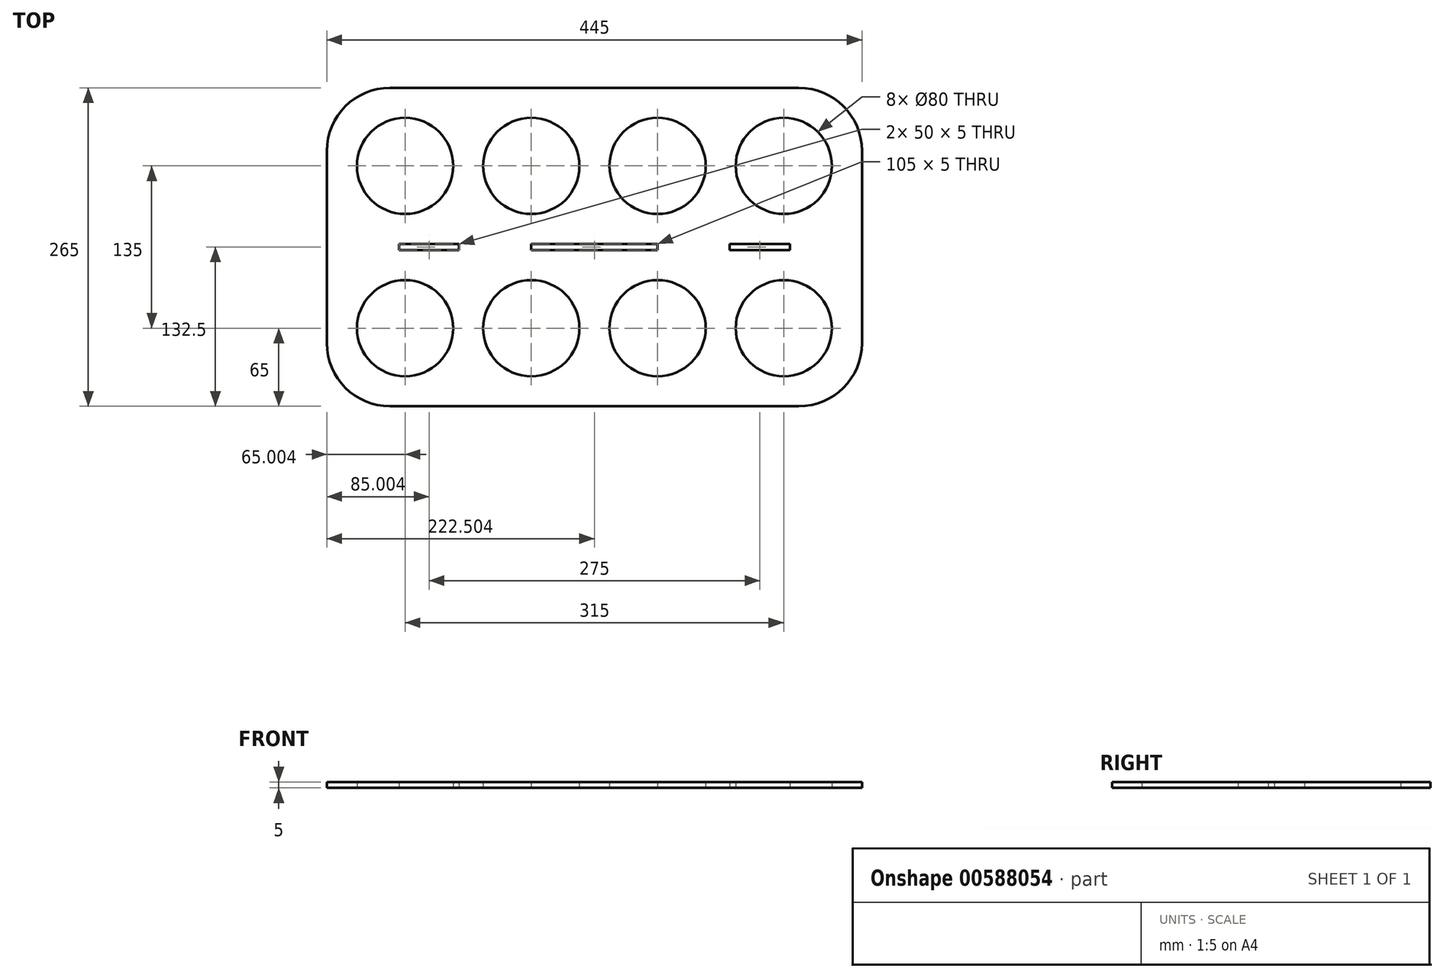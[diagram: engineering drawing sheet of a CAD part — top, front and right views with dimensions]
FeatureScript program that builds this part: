
annotation { "Feature Type Name" : "Feature", "Feature Type Description" : "" }
export const myFeature = defineFeature(function(context is Context, id is Id, definition is map)
    precondition{}
    {
        {
            var Q0;
            Q0=qCreatedBy(makeId("Top.planeOp"),FACE);
            var sketch = newSketch(context, id + "F0", { "sketchPlane" : qUnion([Q0])});
            skLineSegment(sketch, "E0.bottom", {"start": v(-233.99, 135) * mm, "end": v(81.01, 135) * mm, "construction": true});
            skLineSegment(sketch, "E0.top", {"start": v(-233.99, 0) * mm, "end": v(81.01, 0) * mm, "construction": true});
            skLineSegment(sketch, "E0.left", {"start": v(-233.99, 135) * mm, "end": v(-233.99, 0) * mm, "construction": true});
            skLineSegment(sketch, "E0.right", {"start": v(81.01, 135) * mm, "end": v(81.01, 0) * mm, "construction": true});
            skLineSegment(sketch, "E1", {"start": v(-128.99, 135) * mm, "end": v(-128.99, 0) * mm, "construction": true});
            skLineSegment(sketch, "E2", {"start": v(-23.99, 135) * mm, "end": v(-23.99, 0) * mm, "construction": true});
            skLineSegment(sketch, "E3", {"start": v(-233.99, 67.5) * mm, "end": v(81.01, 67.5) * mm, "construction": true});
            skLineSegment(sketch, "E4", {"start": v(-76.49, 135) * mm, "end": v(-76.49, 70) * mm, "construction": true});
            skCircle(sketch, "E5", {"center": v(-233.99, 135) * mm, "radius": 40 * mm});
            skCircle(sketch, "E6", {"center": v(-128.99, 135) * mm, "radius": 40 * mm});
            skCircle(sketch, "E7", {"center": v(-23.99, 135) * mm, "radius": 40 * mm});
            skCircle(sketch, "E8", {"center": v(81.01, 135) * mm, "radius": 40 * mm});
            skCircle(sketch, "E9", {"center": v(-233.99, 0) * mm, "radius": 40 * mm});
            skCircle(sketch, "E10", {"center": v(-128.99, 0) * mm, "radius": 40 * mm});
            skCircle(sketch, "E11", {"center": v(-23.99, 0) * mm, "radius": 40 * mm});
            skCircle(sketch, "E12", {"center": v(81.01, 0) * mm, "radius": 40 * mm});
            skLineSegment(sketch, "E13.bottom", {"start": v(93.51, 200) * mm, "end": v(-246.49, 200) * mm});
            skLineSegment(sketch, "E13.top", {"start": v(93.51, -65) * mm, "end": v(-246.49, -65) * mm});
            skLineSegment(sketch, "E13.left", {"start": v(146.01, 147.5) * mm, "end": v(146.01, 70) * mm});
            skLineSegment(sketch, "E13.right", {"start": v(-298.99, 147.5) * mm, "end": v(-298.99, -12.5) * mm});
            skPoint(sketch, "E13.middle", {"position": v(-76.49, 67.5) * mm});
            skPoint(sketch, "E14.visualSharp", {"position": v(-298.99, 200) * mm});
            skArc(sketch, "E14.filletArc", {"start": v(-246.49, 200) * mm, "mid": v(-283.6, 184.62) * mm, "end": v(-298.99, 147.5) * mm});
            skPoint(sketch, "E15.visualSharp", {"position": v(-298.99, -65) * mm});
            skArc(sketch, "E15.filletArc", {"start": v(-298.99, -12.5) * mm, "mid": v(-283.6, -49.62) * mm, "end": v(-246.49, -65) * mm});
            skPoint(sketch, "E16.visualSharp", {"position": v(146.01, -65) * mm});
            skArc(sketch, "E16.filletArc", {"start": v(93.51, -65) * mm, "mid": v(130.64, -49.62) * mm, "end": v(146.01, -12.5) * mm});
            skPoint(sketch, "E17.visualSharp", {"position": v(146.01, 200) * mm});
            skArc(sketch, "E17.filletArc", {"start": v(146.01, 147.5) * mm, "mid": v(130.64, 184.62) * mm, "end": v(93.51, 200) * mm});
            skPoint(sketch, "E18.right.end.orphan", {"position": v(-298.99, 65) * mm});
            skPoint(sketch, "E18.right.start.orphan", {"position": v(-298.99, 70) * mm});
            skLineSegment(sketch, "E19.trimOffspring", {"start": v(146.01, 65) * mm, "end": v(146.01, -12.5) * mm});
            skLineSegment(sketch, "E20.trimOffspring", {"start": v(-76.49, 65) * mm, "end": v(-76.49, 0) * mm, "construction": true});
            skLineSegment(sketch, "E21", {"start": v(146.01, 70) * mm, "end": v(146.01, 65) * mm});
            skLineSegment(sketch, "E22.bottom", {"start": v(-233.99, 65) * mm, "end": v(-206.48, 65) * mm, "construction": true});
            skLineSegment(sketch, "E22.top", {"start": v(-233.99, 70) * mm, "end": v(-206.48, 70) * mm, "construction": true});
            skLineSegment(sketch, "E22.left", {"start": v(-233.99, 65) * mm, "end": v(-233.99, 70) * mm, "construction": true});
            skLineSegment(sketch, "E22.right", {"start": v(81.01, 65) * mm, "end": v(81.01, 70) * mm, "construction": true});
            skLineSegment(sketch, "E23.bottom", {"start": v(-128.99, 70) * mm, "end": v(-23.99, 70) * mm});
            skLineSegment(sketch, "E23.top", {"start": v(-128.99, 65) * mm, "end": v(-23.99, 65) * mm});
            skLineSegment(sketch, "E23.left", {"start": v(-128.99, 70) * mm, "end": v(-128.99, 65) * mm});
            skLineSegment(sketch, "E23.right", {"start": v(-23.99, 70) * mm, "end": v(-23.99, 65) * mm});
            skLineSegment(sketch, "E24", {"start": v(-233.99, 135) * mm, "end": v(-128.99, 0) * mm, "construction": true});
            skPoint(sketch, "E25.middle", {"position": v(-181.48, 67.5) * mm});
            skLineSegment(sketch, "E26", {"start": v(-23.99, 135) * mm, "end": v(81.01, 0) * mm, "construction": true});
            skLineSegment(sketch, "E27.bottom", {"start": v(36.01, 70) * mm, "end": v(86.01, 70) * mm});
            skLineSegment(sketch, "E27.top", {"start": v(36.01, 65) * mm, "end": v(86.01, 65) * mm});
            skLineSegment(sketch, "E27.left", {"start": v(36.01, 70) * mm, "end": v(36.01, 65) * mm});
            skLineSegment(sketch, "E27.right", {"start": v(86.01, 70) * mm, "end": v(86.01, 65) * mm});
            skPoint(sketch, "E27.middle", {"position": v(28.52, 67.5) * mm});
            skLineSegment(sketch, "E28.trimOffspring", {"start": v(-156.48, 70) * mm, "end": v(81.01, 70) * mm, "construction": true});
            skLineSegment(sketch, "E29.trimOffspring", {"start": v(-156.48, 65) * mm, "end": v(81.01, 65) * mm, "construction": true});
            skLineSegment(sketch, "E30.bottom", {"start": v(-128.99, 135) * mm, "end": v(-298.99, 135) * mm, "construction": true});
            skLineSegment(sketch, "E30.top", {"start": v(-128.99, 0) * mm, "end": v(-298.99, 0) * mm, "construction": true});
            skLineSegment(sketch, "E30.right", {"start": v(-298.99, 135) * mm, "end": v(-298.99, 0) * mm, "construction": true});
            skLineSegment(sketch, "E31", {"start": v(-128.99, 135) * mm, "end": v(-298.99, 0) * mm, "construction": true});
            skLineSegment(sketch, "E32.bottom", {"start": v(-238.99, 70) * mm, "end": v(-188.99, 70) * mm});
            skLineSegment(sketch, "E32.top", {"start": v(-238.99, 65) * mm, "end": v(-188.99, 65) * mm});
            skLineSegment(sketch, "E32.left", {"start": v(-238.99, 70) * mm, "end": v(-238.99, 65) * mm});
            skLineSegment(sketch, "E32.right", {"start": v(-188.99, 70) * mm, "end": v(-188.99, 65) * mm});
            skPoint(sketch, "E32.middle", {"position": v(-213.99, 67.5) * mm});
            skSolve(sketch);
        }
        {
            var Q0;
            Q0 = qSketchRegion(id + "F0", true);
            extrude(context, id + "F1", {"entities" : qUnion([Q0]), "depth" : 5 * mm, "offsetDistance" : 25 * mm});
        }
    });
